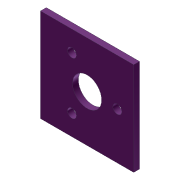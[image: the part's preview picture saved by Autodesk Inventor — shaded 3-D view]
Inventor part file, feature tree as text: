
AUTODESK INVENTOR PART (.ipt)
format: ipt  version: 2012 (Build 160160000, 160)  size: 85,504 bytes
history: native  units: in
note: dims shown in document units (in); Inventor stores cm internally (conversion verified against a paired STEP export)
features: extrude x1, sketch x1
ambient origin geometry x8: Origin, YZ Plane, XZ Plane, XY Plane, X Axis, Y Axis, Z Axis, Center Point
bodies: Solid1 (feature_tree)
feature tree (2):
  extrude  "Extrusion1"  Depth=1.125in
  sketch  "Sketch1"  dims[d0=2.0in d1=1.125in d2=0.625in d3=0.192in d4=0.125in d5=0.0in]
